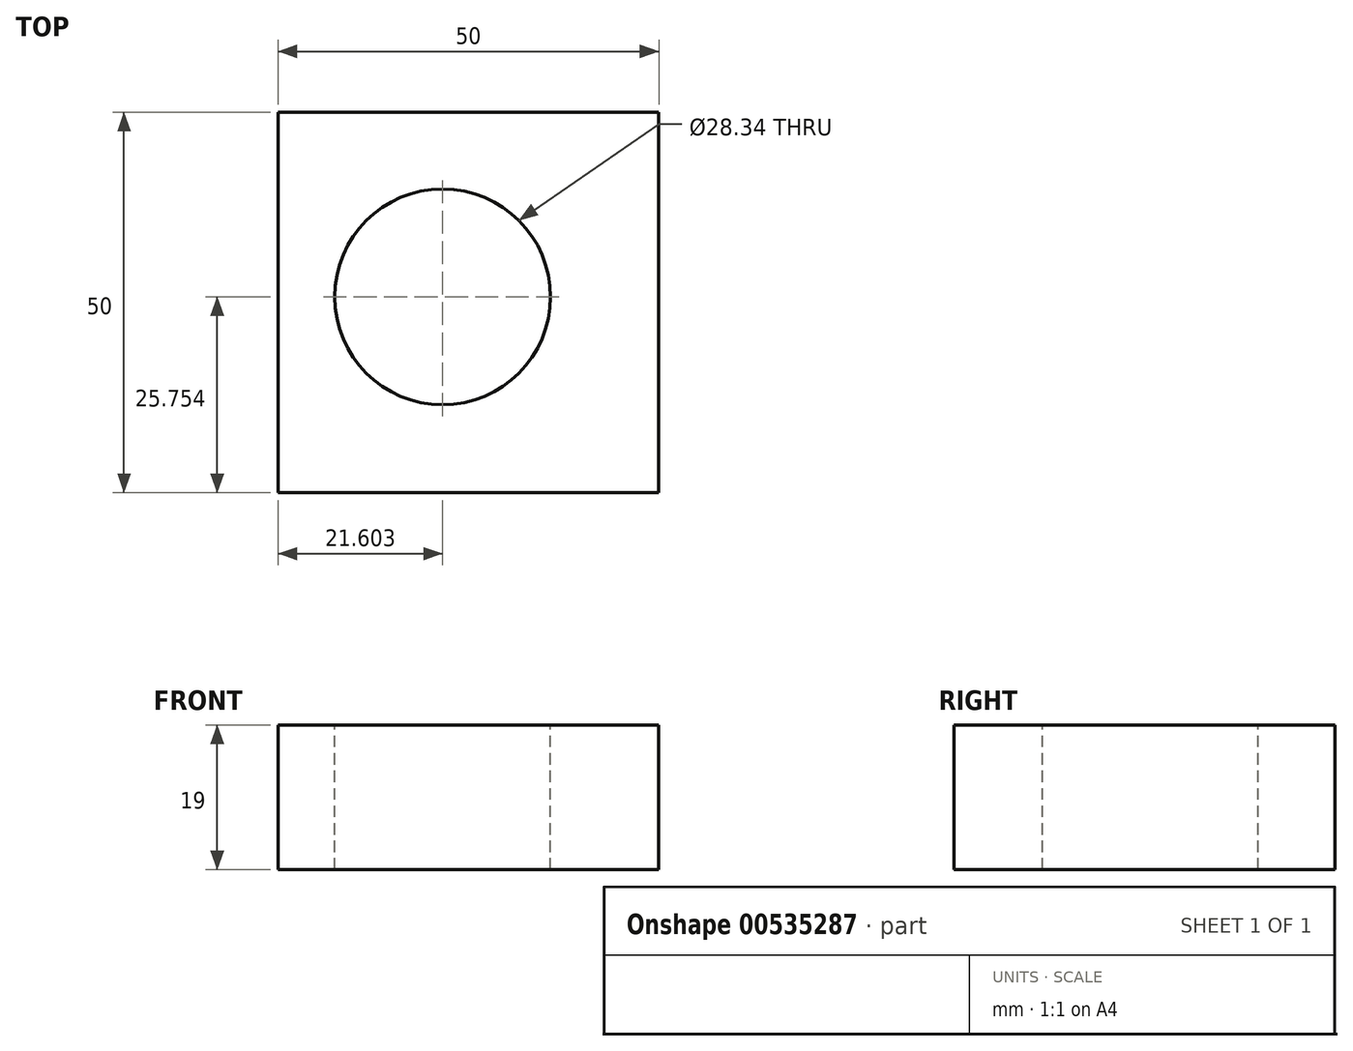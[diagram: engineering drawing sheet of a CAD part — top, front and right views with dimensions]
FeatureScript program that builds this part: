
annotation { "Feature Type Name" : "Feature", "Feature Type Description" : "" }
export const myFeature = defineFeature(function(context is Context, id is Id, definition is map)
    precondition{}
    {
        {
            var Q0;
            Q0=qCreatedBy(makeId("Top.planeOp"),FACE);
            var sketch = newSketch(context, id + "F0", { "sketchPlane" : qUnion([Q0])});
            skLineSegment(sketch, "E0.bottom", {"start": v(-13.46, 20.25) * mm, "end": v(36.54, 20.25) * mm});
            skLineSegment(sketch, "E0.top", {"start": v(-13.46, -29.75) * mm, "end": v(36.54, -29.75) * mm});
            skLineSegment(sketch, "E0.left", {"start": v(-13.46, 20.25) * mm, "end": v(-13.46, -29.75) * mm});
            skLineSegment(sketch, "E0.right", {"start": v(36.54, 20.25) * mm, "end": v(36.54, -29.75) * mm});
            skSolve(sketch);
        }
        {
            var Q0;
            Q0 = qSketchRegion(id + "F0", true);
            extrude(context, id + "F1", {"entities" : qUnion([Q0]), "depth" : 19 * mm, "offsetDistance" : 25 * mm});
        }
        {
            var Q0;
            Q0=makeQuery(id+"F1.opExtrude","CAP_FACE",FACE,{"disambiguationData":[OSD([sQuery(id+"F0.wireOp",EDGE,"E0.bottom"),sQuery(id+"F0.wireOp",EDGE,"E0.top"),sQuery(id+"F0.wireOp",EDGE,"E0.left"),sQuery(id+"F0.wireOp",EDGE,"E0.right")])],"isStart":false});
            var sketch = newSketch(context, id + "F2", { "sketchPlane" : qUnion([Q0])});
            skCircle(sketch, "E1", {"center": v(8.14, -4) * mm, "radius": 14.17 * mm});
            skSolve(sketch);
        }
        {
            var Q0;
            Q0=makeQuery(id+"F2.imprint","IMPRINT",FACE,{"disambiguationData":[TD([[makeQuery(id+"F2.imprint","IMPRINT",EDGE,{"derivedFrom":sQuery(id+"F2.wireOp",EDGE,"E1")}),1.0]])]});
            extrude(context, id + "F3", {"entities" : qUnion([Q0]), "operationType" : NewBodyOperationType.REMOVE, "endBound" : BoundingType.UP_TO_NEXT, "oppositeDirection" : true, "depth" : 19 * mm, "offsetDistance" : 25 * mm});
        }
    });
